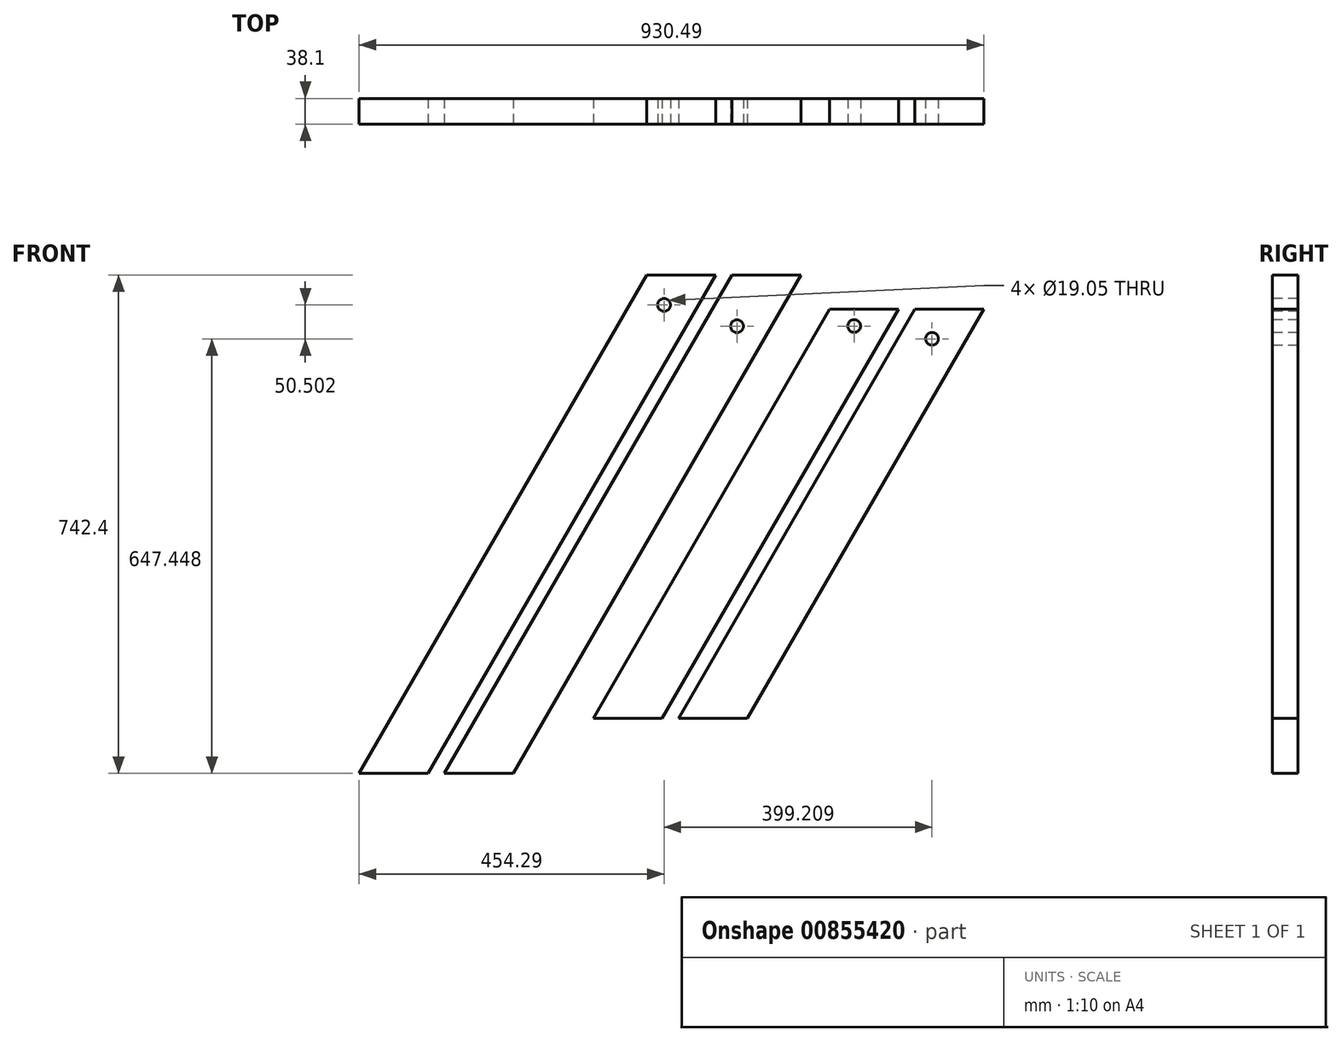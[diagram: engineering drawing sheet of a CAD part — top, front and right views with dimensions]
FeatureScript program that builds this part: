
annotation { "Feature Type Name" : "Feature", "Feature Type Description" : "" }
export const myFeature = defineFeature(function(context is Context, id is Id, definition is map)
    precondition{}
    {
        {
            var Q0;
            Q0=qCreatedBy(makeId("Front.planeOp"),FACE);
            var sketch = newSketch(context, id + "F0", { "sketchPlane" : qUnion([Q0])});
            skLineSegment(sketch, "E0", {"start": v(-454.29, -697.95) * mm, "end": v(-25.66, 44.45) * mm});
            skLineSegment(sketch, "E1", {"start": v(-25.66, 44.45) * mm, "end": v(76.99, 44.45) * mm});
            skLineSegment(sketch, "E2", {"start": v(76.99, 44.45) * mm, "end": v(-351.64, -697.95) * mm});
            skLineSegment(sketch, "E3", {"start": v(-351.64, -697.95) * mm, "end": v(-454.29, -697.95) * mm});
            skLineSegment(sketch, "E4", {"start": v(-351.64, -697.95) * mm, "end": v(173.05, -697.95) * mm});
            skLineSegment(sketch, "E5", {"start": v(-38.5, 22.22) * mm, "end": v(38.5, -22.22) * mm, "construction": true});
            skCircle(sketch, "E6", {"center": v(0, 0) * mm, "radius": 9.53 * mm});
            skSolve(sketch);
        }
        {
            var Q0;
            Q0 = qSketchRegion(id + "F0", true);
            var Q1;
            Q1=makeQuery(id+"F0.imprint","IMPRINT",FACE,{"disambiguationData":[TD([[makeQuery(id+"F0.imprint","IMPRINT",EDGE,{"derivedFrom":sQuery(id+"F0.wireOp",EDGE,"E6")}),1.0]])]});
            extrude(context, id + "F1", {"entities" : qUnion([Q0, Q1]), "oppositeDirection" : true, "depth" : 38.1 * mm, "offsetDistance" : 25.4 * mm});
        }
        {
            var Q0;
            Q0=makeQuery(id+"F1.opExtrude","SWEPT_BODY",BODY,{"disambiguationData":[OSD([sQuery(id+"F0.wireOp",EDGE,"E0"),sQuery(id+"F0.wireOp",EDGE,"E1"),sQuery(id+"F0.wireOp",EDGE,"E2"),sQuery(id+"F0.wireOp",EDGE,"E3"),sQuery(id+"F0.wireOp",EDGE,"E6")])]});
            var Q1;
            Q1=sQuery(id+"F0.wireOp",EDGE,"E4");
            var Q2;
            Q2=sQuery(id+"F0.wireOp",EDGE,"E4");
            transform(context, id + "F2", {"entities" : qUnion([Q0]), "transformType" : TransformType.TRANSLATION_DISTANCE, "transformDirection" : qUnion([Q2]), "distance" : 127 * mm, "makeCopy" : true});
        }
        {
            var Q0;
            Q0=makeQuery(id+"F0.imprint","IMPRINT",FACE,{"disambiguationData":[TD([[makeQuery(id+"F0.imprint","IMPRINT",EDGE,{"derivedFrom":sQuery(id+"F0.wireOp",EDGE,"E6")}),1.0]])]});
            var Q1;
            Q1=sQuery(id+"F0.wireOp",EDGE,"E6");
            var Q2;
            Q2=makeQuery(id+"F1.opExtrude","CAP_FACE",FACE,{"disambiguationData":[OSD([sQuery(id+"F0.wireOp",EDGE,"E0"),sQuery(id+"F0.wireOp",EDGE,"E1"),sQuery(id+"F0.wireOp",EDGE,"E2"),sQuery(id+"F0.wireOp",EDGE,"E3"),sQuery(id+"F0.wireOp",EDGE,"E6")])],"isStart":false});
            extrude(context, id + "F3", {"entities" : qUnion([Q0]), "operationType" : NewBodyOperationType.REMOVE, "surfaceEntities" : qUnion([Q1]), "endBound" : BoundingType.UP_TO_SURFACE, "oppositeDirection" : true, "depth" : 19.05 * mm, "endBoundEntityFace" : qUnion([Q2]), "offsetDistance" : 25.4 * mm});
        }
        {
            var Q0;
            Q0=makeQuery(id+"F2.opPattern","COPY",FACE,{"derivedFrom":makeQuery(id+"F1.opExtrude","CAP_FACE",FACE,{"disambiguationData":[OSD([sQuery(id+"F0.wireOp",EDGE,"E0"),sQuery(id+"F0.wireOp",EDGE,"E1"),sQuery(id+"F0.wireOp",EDGE,"E2"),sQuery(id+"F0.wireOp",EDGE,"E3")])],"isStart":true}),"instanceName":"1"});
            var sketch = newSketch(context, id + "F4", { "sketchPlane" : qUnion([Q0])});
            skLineSegment(sketch, "E7", {"start": v(70.17, -9.53) * mm, "end": v(147.16, -53.98) * mm, "construction": true});
            skCircle(sketch, "E8", {"center": v(108.67, -31.75) * mm, "radius": 9.53 * mm});
            skSolve(sketch);
        }
        {
            var Q0;
            Q0=makeQuery(id+"F4.imprint","IMPRINT",FACE,{"disambiguationData":[TD([[makeQuery(id+"F4.imprint","IMPRINT",EDGE,{"derivedFrom":sQuery(id+"F4.wireOp",EDGE,"E8")}),1.0]])]});
            var Q1;
            Q1=sQuery(id+"F4.wireOp",EDGE,"E8");
            extrude(context, id + "F5", {"entities" : qUnion([Q0]), "operationType" : NewBodyOperationType.REMOVE, "surfaceEntities" : qUnion([Q1]), "oppositeDirection" : true, "depth" : 38.1 * mm, "offsetDistance" : 25.4 * mm});
        }
        {
            var Q0;
            Q0=qCreatedBy(makeId("Front.planeOp"),FACE);
            var sketch = newSketch(context, id + "F6", { "sketchPlane" : qUnion([Q0])});
            skLineSegment(sketch, "E9", {"start": v(-105.4, -615.65) * mm, "end": v(246.55, -6.05) * mm});
            skLineSegment(sketch, "E10", {"start": v(246.55, -6.05) * mm, "end": v(349.2, -6.05) * mm});
            skLineSegment(sketch, "E11", {"start": v(349.2, -6.05) * mm, "end": v(-2.75, -615.65) * mm});
            skLineSegment(sketch, "E12", {"start": v(-2.75, -615.65) * mm, "end": v(-105.4, -615.65) * mm});
            skLineSegment(sketch, "E13", {"start": v(-2.75, -615.65) * mm, "end": v(523.76, -615.65) * mm});
            skLineSegment(sketch, "E14", {"start": v(244.71, -9.23) * mm, "end": v(321.7, -53.68) * mm, "construction": true});
            skCircle(sketch, "E15", {"center": v(283.2, -31.45) * mm, "radius": 9.53 * mm});
            skSolve(sketch);
        }
        {
            var Q0;
            Q0=makeQuery(id+"F6.imprint","IMPRINT",FACE,{"disambiguationData":[TD([[makeQuery(id+"F6.imprint","IMPRINT",EDGE,{"derivedFrom":sQuery(id+"F6.wireOp",EDGE,"E9")}),-1.0]])]});
            var Q1;
            Q1=makeQuery(id+"F6.imprint","IMPRINT",FACE,{"disambiguationData":[TD([[makeQuery(id+"F6.imprint","IMPRINT",EDGE,{"derivedFrom":sQuery(id+"F6.wireOp",EDGE,"E15")}),1.0]])]});
            extrude(context, id + "F7", {"entities" : qUnion([Q0, Q1]), "oppositeDirection" : true, "depth" : 38.1 * mm, "offsetDistance" : 25.4 * mm});
        }
        {
            var Q0;
            Q0=makeQuery(id+"F7.opExtrude","SWEPT_BODY",BODY,{"disambiguationData":[OSD([sQuery(id+"F6.wireOp",EDGE,"E9"),sQuery(id+"F6.wireOp",EDGE,"E10"),sQuery(id+"F6.wireOp",EDGE,"E11"),sQuery(id+"F6.wireOp",EDGE,"E12")])]});
            var Q1;
            Q1=sQuery(id+"F6.wireOp",EDGE,"E13");
            transform(context, id + "F8", {"entities" : qUnion([Q0]), "transformType" : TransformType.TRANSLATION_DISTANCE, "transformDirection" : qUnion([Q1]), "distance" : 127 * mm, "makeCopy" : true});
        }
        {
            var Q0;
            Q0=makeQuery(id+"F6.imprint","IMPRINT",FACE,{"disambiguationData":[TD([[makeQuery(id+"F6.imprint","IMPRINT",EDGE,{"derivedFrom":sQuery(id+"F6.wireOp",EDGE,"E15")}),1.0]])]});
            extrude(context, id + "F9", {"entities" : qUnion([Q0]), "operationType" : NewBodyOperationType.REMOVE, "oppositeDirection" : true, "depth" : 38.1 * mm, "offsetDistance" : 25.4 * mm});
        }
        {
            var Q0;
            Q0=makeQuery(id+"F8.opPattern","COPY",FACE,{"derivedFrom":makeQuery(id+"F7.opExtrude","CAP_FACE",FACE,{"disambiguationData":[OSD([sQuery(id+"F6.wireOp",EDGE,"E9"),sQuery(id+"F6.wireOp",EDGE,"E10"),sQuery(id+"F6.wireOp",EDGE,"E11"),sQuery(id+"F6.wireOp",EDGE,"E12")])],"isStart":true}),"instanceName":"1"});
            var sketch = newSketch(context, id + "F10", { "sketchPlane" : qUnion([Q0])});
            skLineSegment(sketch, "E16", {"start": v(360.71, -28.28) * mm, "end": v(437.7, -72.73) * mm, "construction": true});
            skCircle(sketch, "E17", {"center": v(399.2, -50.5) * mm, "radius": 9.53 * mm});
            skSolve(sketch);
        }
        {
            var Q0;
            Q0=makeQuery(id+"F10.imprint","IMPRINT",FACE,{"disambiguationData":[TD([[makeQuery(id+"F10.imprint","IMPRINT",EDGE,{"derivedFrom":sQuery(id+"F10.wireOp",EDGE,"E17")}),1.0]])]});
            extrude(context, id + "F11", {"entities" : qUnion([Q0]), "operationType" : NewBodyOperationType.REMOVE, "oppositeDirection" : true, "depth" : 38.1 * mm, "offsetDistance" : 25.4 * mm});
        }
    });
